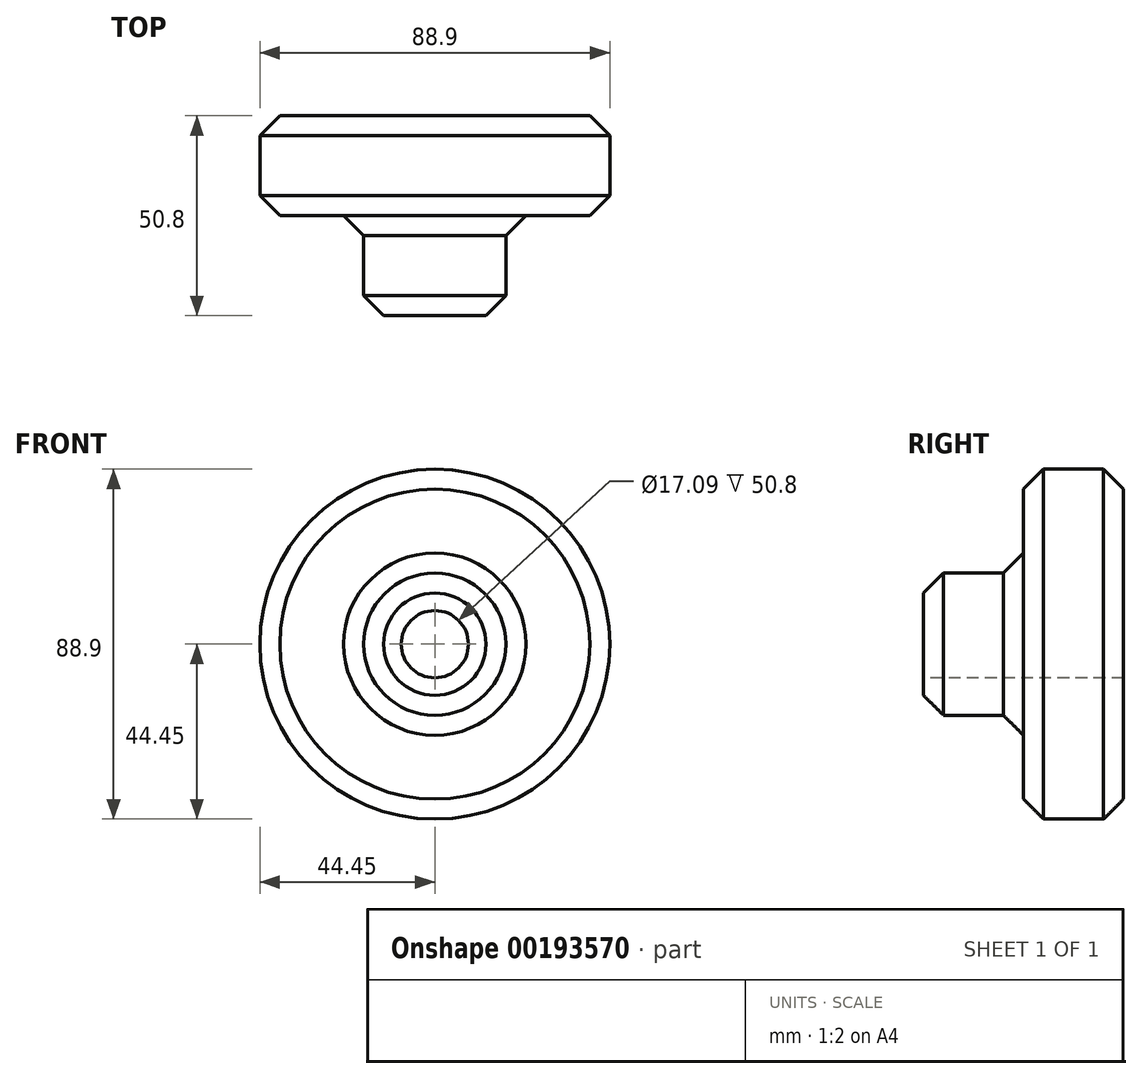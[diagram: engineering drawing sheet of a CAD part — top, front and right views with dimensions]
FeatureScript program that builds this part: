
annotation { "Feature Type Name" : "Feature", "Feature Type Description" : "" }
export const myFeature = defineFeature(function(context is Context, id is Id, definition is map)
    precondition{}
    {
        {
            var Q0;
            Q0=qCreatedBy(makeId("Front.planeOp"),FACE);
            var sketch = newSketch(context, id + "F0", { "sketchPlane" : qUnion([Q0])});
            skCircle(sketch, "E0", {"center": v(0, 0) * mm, "radius": 44.45 * mm});
            skSolve(sketch);
        }
        {
            var Q0;
            Q0=makeQuery(id+"F0.imprint","IMPRINT",FACE,{"disambiguationData":[TD([[makeQuery(id+"F0.imprint","IMPRINT",EDGE,{"derivedFrom":sQuery(id+"F0.wireOp",EDGE,"E0")}),1.0]])]});
            extrude(context, id + "F1", {"entities" : qUnion([Q0]), "depth" : 25.4 * mm});
        }
        {
            var Q0;
            Q0=qCreatedBy(makeId("Front.planeOp"),FACE);
            var sketch = newSketch(context, id + "F2", { "sketchPlane" : qUnion([Q0])});
            skCircle(sketch, "E1", {"center": v(0, 0) * mm, "radius": 18.08 * mm});
            skSolve(sketch);
        }
        {
            var Q0;
            Q0 = qSketchRegion(id + "F2", true);
            extrude(context, id + "F3", {"entities" : qUnion([Q0]), "operationType" : NewBodyOperationType.ADD, "depth" : 50.8 * mm});
        }
        {
            var Q0;
            Q0=makeQuery(id+"F3.opExtrude","CAP_FACE",FACE,{"disambiguationData":[OSD([sQuery(id+"F2.wireOp",EDGE,"E1")])],"isStart":false});
            var sketch = newSketch(context, id + "F4", { "sketchPlane" : qUnion([Q0])});
            skCircle(sketch, "E2", {"center": v(0, 0) * mm, "radius": 8.55 * mm});
            skSolve(sketch);
        }
        {
            var Q0;
            Q0=makeQuery(id+"F4.imprint","IMPRINT",FACE,{"disambiguationData":[TD([[makeQuery(id+"F4.imprint","IMPRINT",EDGE,{"derivedFrom":sQuery(id+"F4.wireOp",EDGE,"E2")}),1.0]])]});
            extrude(context, id + "F5", {"entities" : qUnion([Q0]), "operationType" : NewBodyOperationType.REMOVE, "oppositeDirection" : true, "depth" : 127 * mm});
        }
        {
            var Q0;
            Q0=makeQuery(id+"F3.opExtrude","SWEPT_FACE",FACE,{"disambiguationData":[OSD([sQuery(id+"F2.wireOp",EDGE,"E1")])]});
            chamfer(context, id + "F6", {"entities" : qUnion([Q0]), "width" : 5.08 * mm, "tangentPropagation" : true});
        }
        {
            var Q0;
            Q0=makeQuery(id+"F1.opExtrude","SWEPT_FACE",FACE,{"disambiguationData":[OSD([sQuery(id+"F0.wireOp",EDGE,"E0")])]});
            chamfer(context, id + "F7", {"entities" : qUnion([Q0]), "width" : 5.08 * mm, "tangentPropagation" : true});
        }
    });
